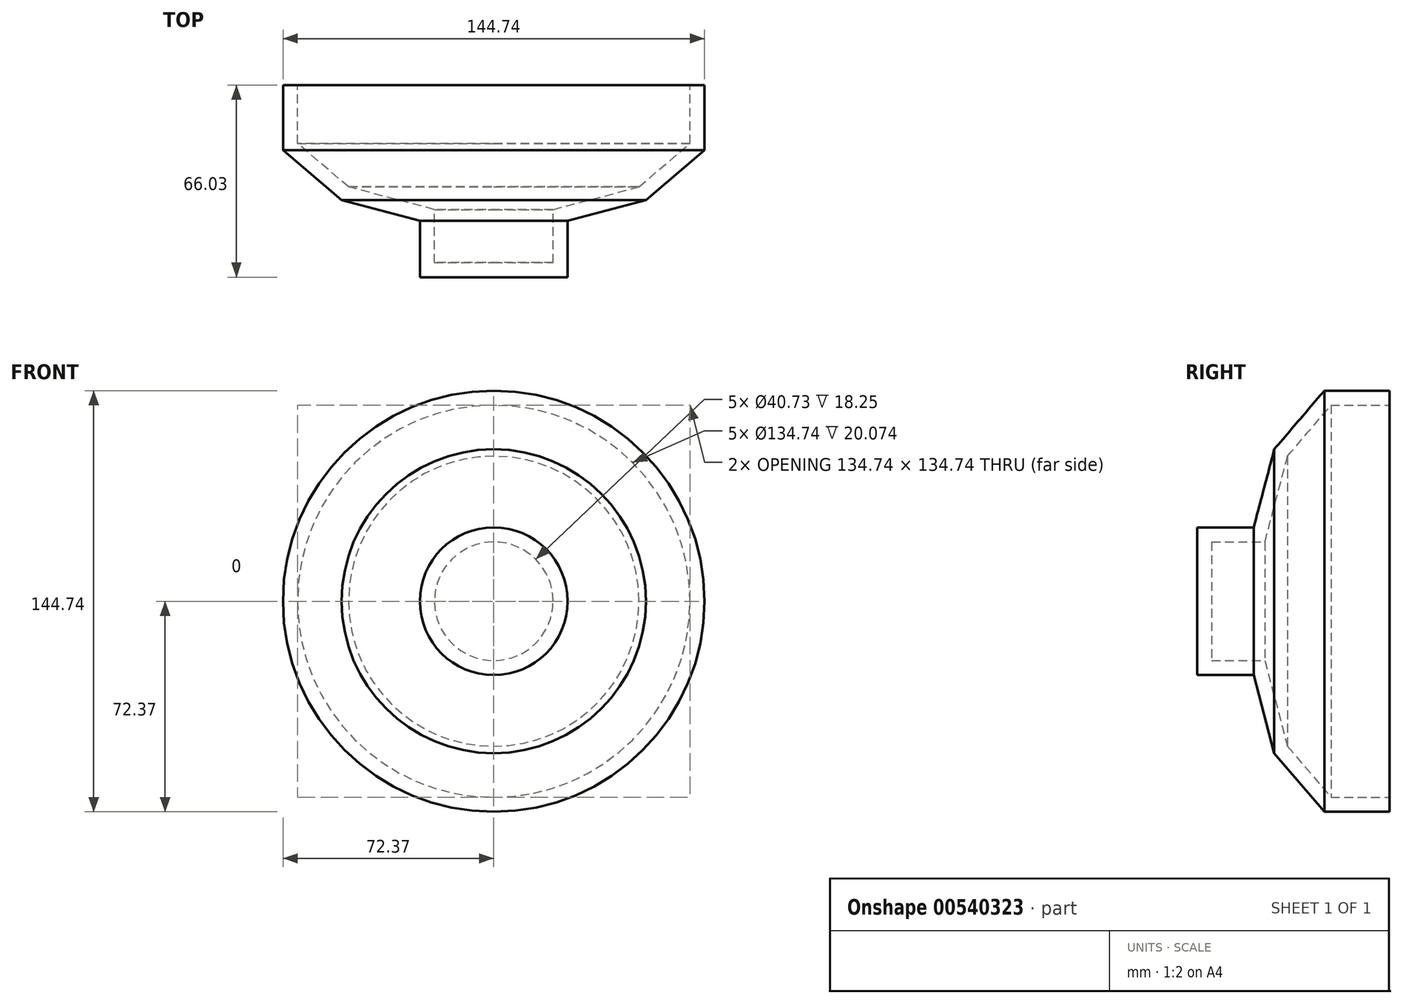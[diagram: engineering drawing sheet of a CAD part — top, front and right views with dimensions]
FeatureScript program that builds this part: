
annotation { "Feature Type Name" : "Feature", "Feature Type Description" : "" }
export const myFeature = defineFeature(function(context is Context, id is Id, definition is map)
    precondition{}
    {
        {
            var Q0;
            Q0=qCreatedBy(makeId("Top.planeOp"),FACE);
            var sketch = newSketch(context, id + "F0", { "sketchPlane" : qUnion([Q0])});
            skLineSegment(sketch, "E0", {"start": v(-25.37, 0) * mm, "end": v(-25.37, 19.4) * mm});
            skLineSegment(sketch, "E1", {"start": v(-25.37, 19.4) * mm, "end": v(-52.23, 26.49) * mm});
            skLineSegment(sketch, "E2", {"start": v(-52.23, 26.49) * mm, "end": v(-72.37, 43.65) * mm});
            skLineSegment(sketch, "E3", {"start": v(-72.37, 43.65) * mm, "end": v(-72.37, 66.03) * mm});
            skLineSegment(sketch, "E4", {"start": v(-72.37, 66.03) * mm, "end": v(0, 66.03) * mm});
            skLineSegment(sketch, "E5", {"start": v(0, 66.03) * mm, "end": v(0, 0) * mm});
            skLineSegment(sketch, "E6", {"start": v(0, 0) * mm, "end": v(-25.37, 0) * mm});
            skSolve(sketch);
        }
        {
            var Q0;
            Q0=makeQuery(id+"F0.imprint","IMPRINT",FACE,{"disambiguationData":[TD([[makeQuery(id+"F0.imprint","IMPRINT",EDGE,{"derivedFrom":sQuery(id+"F0.wireOp",EDGE,"E0")}),-1.0]])]});
            var Q1;
            Q1=sQuery(id+"F0.wireOp",EDGE,"E5");
            revolve(context, id + "F1", {"entities" : qUnion([Q0]), "axis" : qUnion([Q1]), "revolveType" : RevolveType.FULL});
        }
        {
            var Q0;
            Q0=makeQuery(id+"F1.opRevolve","SWEPT_FACE",FACE,{"disambiguationData":[OSD([sQuery(id+"F0.wireOp",EDGE,"E4")])]});
            shell(context, id + "F2", {"entities" : qUnion([Q0]), "thickness" : 5 * mm});
        }
    });
